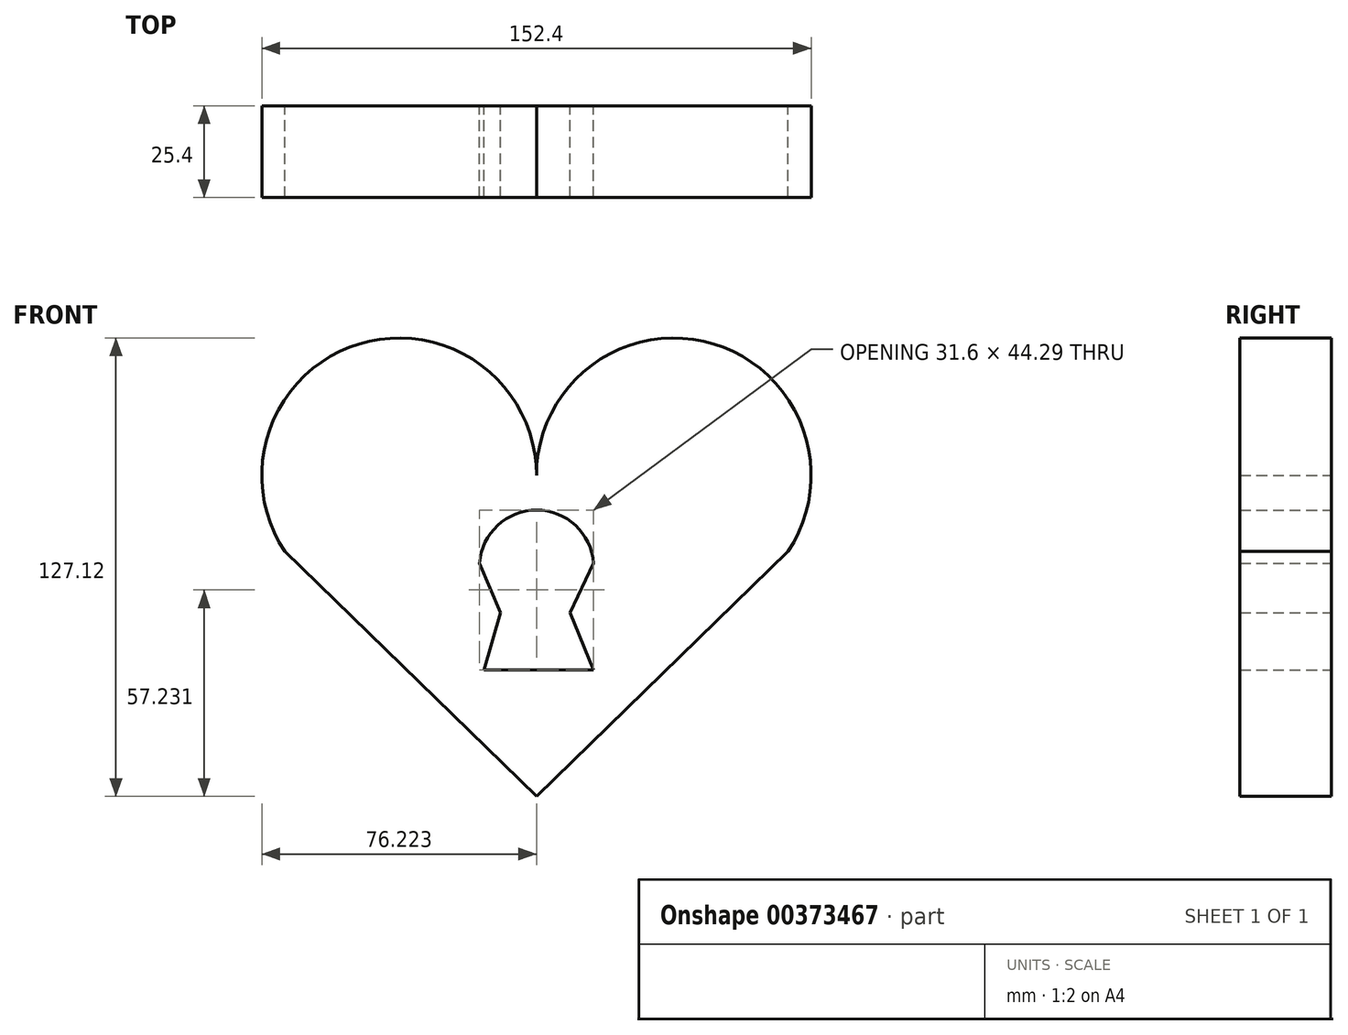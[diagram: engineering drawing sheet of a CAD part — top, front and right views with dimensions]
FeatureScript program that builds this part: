
annotation { "Feature Type Name" : "Feature", "Feature Type Description" : "" }
export const myFeature = defineFeature(function(context is Context, id is Id, definition is map)
    precondition{}
    {
        {
            var Q0;
            Q0=qCreatedBy(makeId("Front.planeOp"),FACE);
            var sketch = newSketch(context, id + "F0", { "sketchPlane" : qUnion([Q0])});
            skArc(sketch, "E0", {"start": v(0, 38.1) * mm, "mid": v(-49.14, 74.56) * mm, "end": v(-69.8, 16.96) * mm});
            skArc(sketch, "E1", {"start": v(69.8, 16.96) * mm, "mid": v(49.14, 74.56) * mm, "end": v(0, 38.1) * mm});
            skLineSegment(sketch, "E2", {"start": v(69.8, 16.96) * mm, "end": v(0, -50.92) * mm});
            skLineSegment(sketch, "E3", {"start": v(0, -50.92) * mm, "end": v(-69.8, 16.96) * mm});
            skArc(sketch, "E4", {"start": v(15.82, 13.7) * mm, "mid": v(0.02, 28.46) * mm, "end": v(-15.78, 13.7) * mm});
            skLineSegment(sketch, "E5", {"start": v(15.82, 13.7) * mm, "end": v(9.38, 0) * mm});
            skLineSegment(sketch, "E6", {"start": v(9.38, 0) * mm, "end": v(15.82, -15.84) * mm});
            skLineSegment(sketch, "E7", {"start": v(-15.78, 13.7) * mm, "end": v(-9.94, 0) * mm});
            skLineSegment(sketch, "E8", {"start": v(15.82, -15.84) * mm, "end": v(-14.53, -15.84) * mm});
            skLineSegment(sketch, "E9", {"start": v(-9.94, 0) * mm, "end": v(-14.53, -15.84) * mm});
            skSolve(sketch);
        }
        {
            var Q0;
            Q0=makeQuery(id+"F0.imprint","IMPRINT",FACE,{"disambiguationData":[TD([[makeQuery(id+"F0.imprint","IMPRINT",EDGE,{"derivedFrom":sQuery(id+"F0.wireOp",EDGE,"E0")}),1.0]])]});
            extrude(context, id + "F1", {"entities" : qUnion([Q0]), "depth" : 25.4 * mm});
        }
    });
